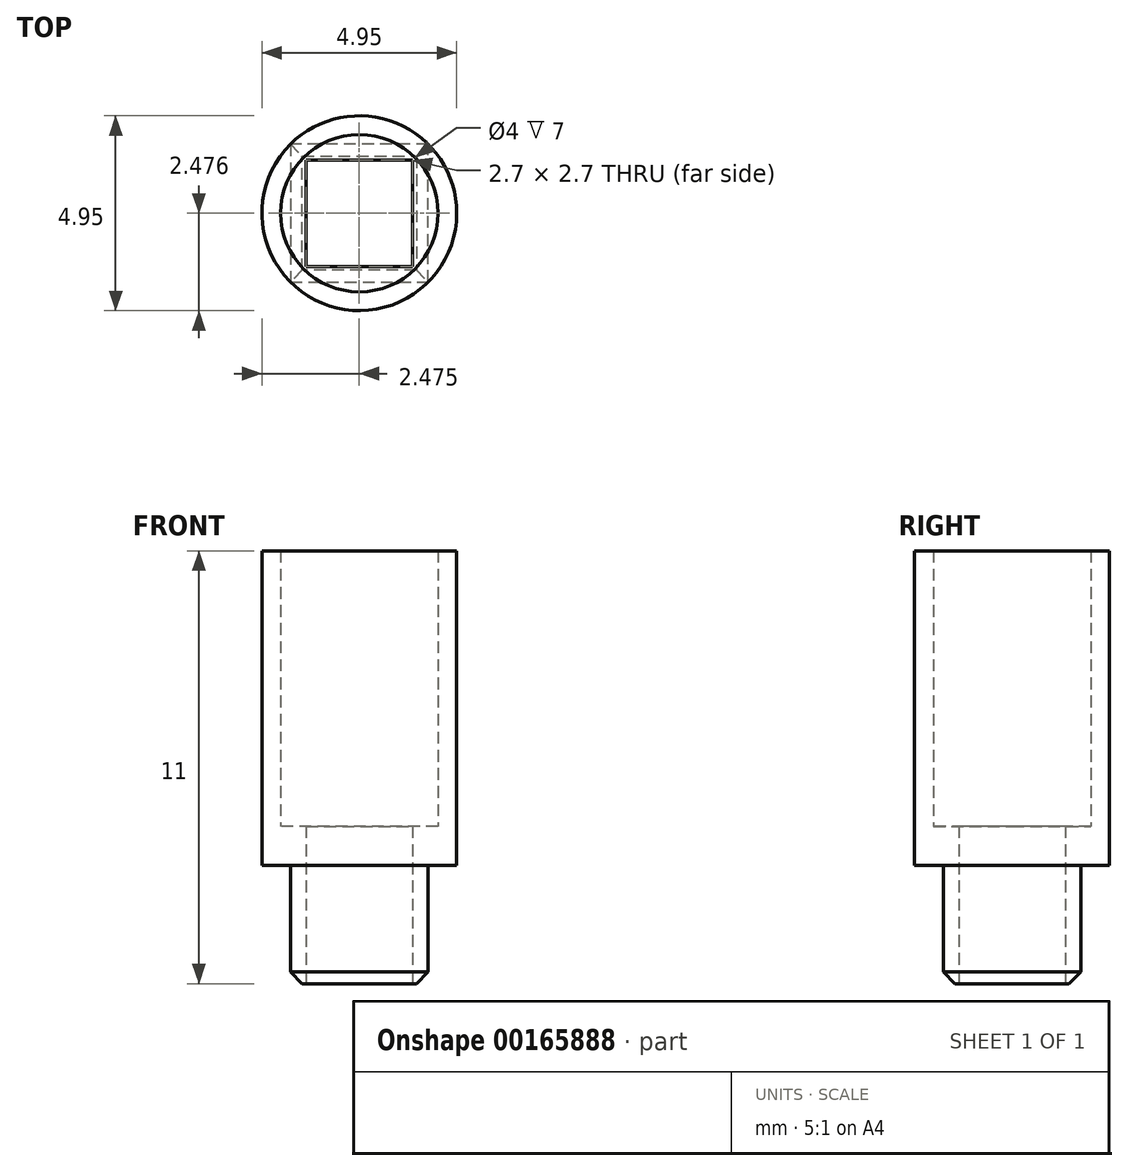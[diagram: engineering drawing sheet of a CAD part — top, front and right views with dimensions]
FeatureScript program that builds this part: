
annotation { "Feature Type Name" : "Feature", "Feature Type Description" : "" }
export const myFeature = defineFeature(function(context is Context, id is Id, definition is map)
    precondition{}
    {
        {
            var Q0;
            Q0=qCreatedBy(makeId("Top.planeOp"),FACE);
            var sketch = newSketch(context, id + "F0", { "sketchPlane" : qUnion([Q0])});
            skLineSegment(sketch, "E0.bottom", {"start": v(7.4, -10.31) * mm, "end": v(10.1, -10.31) * mm});
            skLineSegment(sketch, "E0.top", {"start": v(7.4, -13.01) * mm, "end": v(10.1, -13.01) * mm});
            skLineSegment(sketch, "E0.left", {"start": v(7.4, -10.31) * mm, "end": v(7.4, -13.01) * mm});
            skLineSegment(sketch, "E0.right", {"start": v(10.1, -10.31) * mm, "end": v(10.1, -13.01) * mm});
            skLineSegment(sketch, "E1.bottom", {"start": v(7, -9.91) * mm, "end": v(10.5, -9.91) * mm});
            skLineSegment(sketch, "E1.top", {"start": v(7, -13.41) * mm, "end": v(10.5, -13.41) * mm});
            skLineSegment(sketch, "E1.left", {"start": v(7, -9.91) * mm, "end": v(7, -13.41) * mm});
            skLineSegment(sketch, "E1.right", {"start": v(10.5, -9.91) * mm, "end": v(10.5, -13.41) * mm});
            skSolve(sketch);
        }
        {
            var Q0;
            Q0 = qSketchRegion(id + "F0", true);
            extrude(context, id + "F1", {"entities" : qUnion([Q0]), "depth" : 4 * mm});
        }
        {
            var Q0;
            Q0=makeQuery(id+"F1.opExtrude","CAP_FACE",FACE,{"disambiguationData":[OSD([sQuery(id+"F0.wireOp",EDGE,"E0.bottom"),sQuery(id+"F0.wireOp",EDGE,"E0.top"),sQuery(id+"F0.wireOp",EDGE,"E0.left"),sQuery(id+"F0.wireOp",EDGE,"E0.right"),sQuery(id+"F0.wireOp",EDGE,"E1.bottom"),sQuery(id+"F0.wireOp",EDGE,"E1.top"),sQuery(id+"F0.wireOp",EDGE,"E1.left"),sQuery(id+"F0.wireOp",EDGE,"E1.right")])],"isStart":false});
            var sketch = newSketch(context, id + "F2", { "sketchPlane" : qUnion([Q0])});
            skCircle(sketch, "E2", {"center": v(8.75, -11.66) * mm, "radius": 2 * mm});
            skPoint(sketch, "E2.centerSnap0", {"position": v(10.1, -11.66) * mm});
            skPoint(sketch, "E2.centerSnap1", {"position": v(8.75, -13.01) * mm});
            skCircle(sketch, "E3", {"center": v(8.75, -11.66) * mm, "radius": 2.47 * mm});
            skSolve(sketch);
        }
        {
            var Q0;
            Q0 = qSketchRegion(id + "F2", true);
            extrude(context, id + "F3", {"entities" : qUnion([Q0]), "operationType" : NewBodyOperationType.ADD, "depth" : 7 * mm});
        }
        {
            var Q0;
            {var subQ0=sQuery(id+"F2.wireOp",EDGE,"E2");var subQ1=makeQuery(id+"F1.opExtrude","CAP_EDGE",EDGE,{"disambiguationData":[OSD([sQuery(id+"F0.wireOp",EDGE,"E1.right")])],"isStart":false});var subQ2=makeQuery(id+"F2.imprint","INTERSECT",VERTEX,{"disambiguationData":[OD(0.0)],"derivedFrom":[subQ1,subQ0]});Q0=makeQuery(id+"F2.imprint","IMPRINT",FACE,{"disambiguationData":[TD([[makeQuery(id+"F2.imprint","IMPRINT",EDGE,{"disambiguationData":[TD([[subQ2,1.0]])],"derivedFrom":subQ0}),-1.0]])]});}
            var Q1;
            {var subQ0=sQuery(id+"F2.wireOp",EDGE,"E2");var subQ1=makeQuery(id+"F1.opExtrude","CAP_EDGE",EDGE,{"disambiguationData":[OSD([sQuery(id+"F0.wireOp",EDGE,"E1.right")])],"isStart":false});var subQ2=makeQuery(id+"F2.imprint","INTERSECT",VERTEX,{"disambiguationData":[OD(0.0)],"derivedFrom":[subQ1,subQ0]});Q1=makeQuery(id+"F2.imprint","IMPRINT",FACE,{"disambiguationData":[TD([[makeQuery(id+"F2.imprint","IMPRINT",EDGE,{"disambiguationData":[TD([[subQ2,1.0]])],"derivedFrom":subQ0}),1.0]])]});}
            var Q2;
            {var subQ0=sQuery(id+"F2.wireOp",EDGE,"E2");var subQ1=makeQuery(id+"F1.opExtrude","CAP_EDGE",EDGE,{"disambiguationData":[OSD([sQuery(id+"F0.wireOp",EDGE,"E1.bottom")])],"isStart":false});var subQ2=makeQuery(id+"F2.imprint","INTERSECT",VERTEX,{"disambiguationData":[OD(0.0)],"derivedFrom":[subQ1,subQ0]});Q2=makeQuery(id+"F2.imprint","IMPRINT",FACE,{"disambiguationData":[TD([[makeQuery(id+"F2.imprint","IMPRINT",EDGE,{"disambiguationData":[TD([[subQ2,-1.0]])],"derivedFrom":subQ0}),-1.0]])]});}
            var Q3;
            {var subQ0=sQuery(id+"F2.wireOp",EDGE,"E2");var subQ1=makeQuery(id+"F1.opExtrude","CAP_EDGE",EDGE,{"disambiguationData":[OSD([sQuery(id+"F0.wireOp",EDGE,"E1.bottom")])],"isStart":false});var subQ2=makeQuery(id+"F2.imprint","INTERSECT",VERTEX,{"disambiguationData":[OD(0.0)],"derivedFrom":[subQ1,subQ0]});Q3=makeQuery(id+"F2.imprint","IMPRINT",FACE,{"disambiguationData":[TD([[makeQuery(id+"F2.imprint","IMPRINT",EDGE,{"disambiguationData":[TD([[subQ2,-1.0]])],"derivedFrom":subQ0}),1.0]])]});}
            var Q4;
            {var subQ0=sQuery(id+"F2.wireOp",EDGE,"E2");var subQ1=makeQuery(id+"F1.opExtrude","CAP_EDGE",EDGE,{"disambiguationData":[OSD([sQuery(id+"F0.wireOp",EDGE,"E1.left")])],"isStart":false});var subQ2=makeQuery(id+"F2.imprint","INTERSECT",VERTEX,{"disambiguationData":[OD(0.0)],"derivedFrom":[subQ1,subQ0]});Q4=makeQuery(id+"F2.imprint","IMPRINT",FACE,{"disambiguationData":[TD([[makeQuery(id+"F2.imprint","IMPRINT",EDGE,{"disambiguationData":[TD([[subQ2,-1.0]])],"derivedFrom":subQ0}),-1.0]])]});}
            var Q5;
            {var subQ0=sQuery(id+"F2.wireOp",EDGE,"E2");var subQ1=makeQuery(id+"F1.opExtrude","CAP_EDGE",EDGE,{"disambiguationData":[OSD([sQuery(id+"F0.wireOp",EDGE,"E1.left")])],"isStart":false});var subQ2=makeQuery(id+"F2.imprint","INTERSECT",VERTEX,{"disambiguationData":[OD(0.0)],"derivedFrom":[subQ1,subQ0]});Q5=makeQuery(id+"F2.imprint","IMPRINT",FACE,{"disambiguationData":[TD([[makeQuery(id+"F2.imprint","IMPRINT",EDGE,{"disambiguationData":[TD([[subQ2,-1.0]])],"derivedFrom":subQ0}),1.0]])]});}
            var Q6;
            {var subQ0=sQuery(id+"F2.wireOp",EDGE,"E2");var subQ1=makeQuery(id+"F1.opExtrude","CAP_EDGE",EDGE,{"disambiguationData":[OSD([sQuery(id+"F0.wireOp",EDGE,"E1.top")])],"isStart":false});var subQ2=makeQuery(id+"F2.imprint","INTERSECT",VERTEX,{"disambiguationData":[OD(0.0)],"derivedFrom":[subQ1,subQ0]});Q6=makeQuery(id+"F2.imprint","IMPRINT",FACE,{"disambiguationData":[TD([[makeQuery(id+"F2.imprint","IMPRINT",EDGE,{"disambiguationData":[TD([[subQ2,-1.0]])],"derivedFrom":subQ0}),-1.0]])]});}
            var Q7;
            {var subQ0=sQuery(id+"F2.wireOp",EDGE,"E2");var subQ1=makeQuery(id+"F1.opExtrude","CAP_EDGE",EDGE,{"disambiguationData":[OSD([sQuery(id+"F0.wireOp",EDGE,"E1.top")])],"isStart":false});var subQ2=makeQuery(id+"F2.imprint","INTERSECT",VERTEX,{"disambiguationData":[OD(0.0)],"derivedFrom":[subQ1,subQ0]});Q7=makeQuery(id+"F2.imprint","IMPRINT",FACE,{"disambiguationData":[TD([[makeQuery(id+"F2.imprint","IMPRINT",EDGE,{"disambiguationData":[TD([[subQ2,-1.0]])],"derivedFrom":subQ0}),1.0]])]});}
            extrude(context, id + "F4", {"entities" : qUnion([Q0, Q1, Q2, Q3, Q4, Q5, Q6, Q7]), "operationType" : NewBodyOperationType.ADD, "oppositeDirection" : true, "depth" : 1 * mm});
        }
        {
            var Q0;
            Q0=makeQuery(id+"F1.opExtrude","CAP_EDGE",EDGE,{"disambiguationData":[OSD([sQuery(id+"F0.wireOp",EDGE,"E1.right")])],"isStart":true});
            var Q1;
            Q1=makeQuery(id+"F1.opExtrude","CAP_EDGE",EDGE,{"disambiguationData":[OSD([sQuery(id+"F0.wireOp",EDGE,"E1.bottom")])],"isStart":true});
            var Q2;
            Q2=makeQuery(id+"F1.opExtrude","CAP_EDGE",EDGE,{"disambiguationData":[OSD([sQuery(id+"F0.wireOp",EDGE,"E1.left")])],"isStart":true});
            var Q3;
            Q3=makeQuery(id+"F1.opExtrude","CAP_EDGE",EDGE,{"disambiguationData":[OSD([sQuery(id+"F0.wireOp",EDGE,"E1.top")])],"isStart":true});
            chamfer(context, id + "F5", {"entities" : qUnion([Q0, Q1, Q2, Q3]), "width" : 0.3 * mm, "tangentPropagation" : true});
        }
    });
